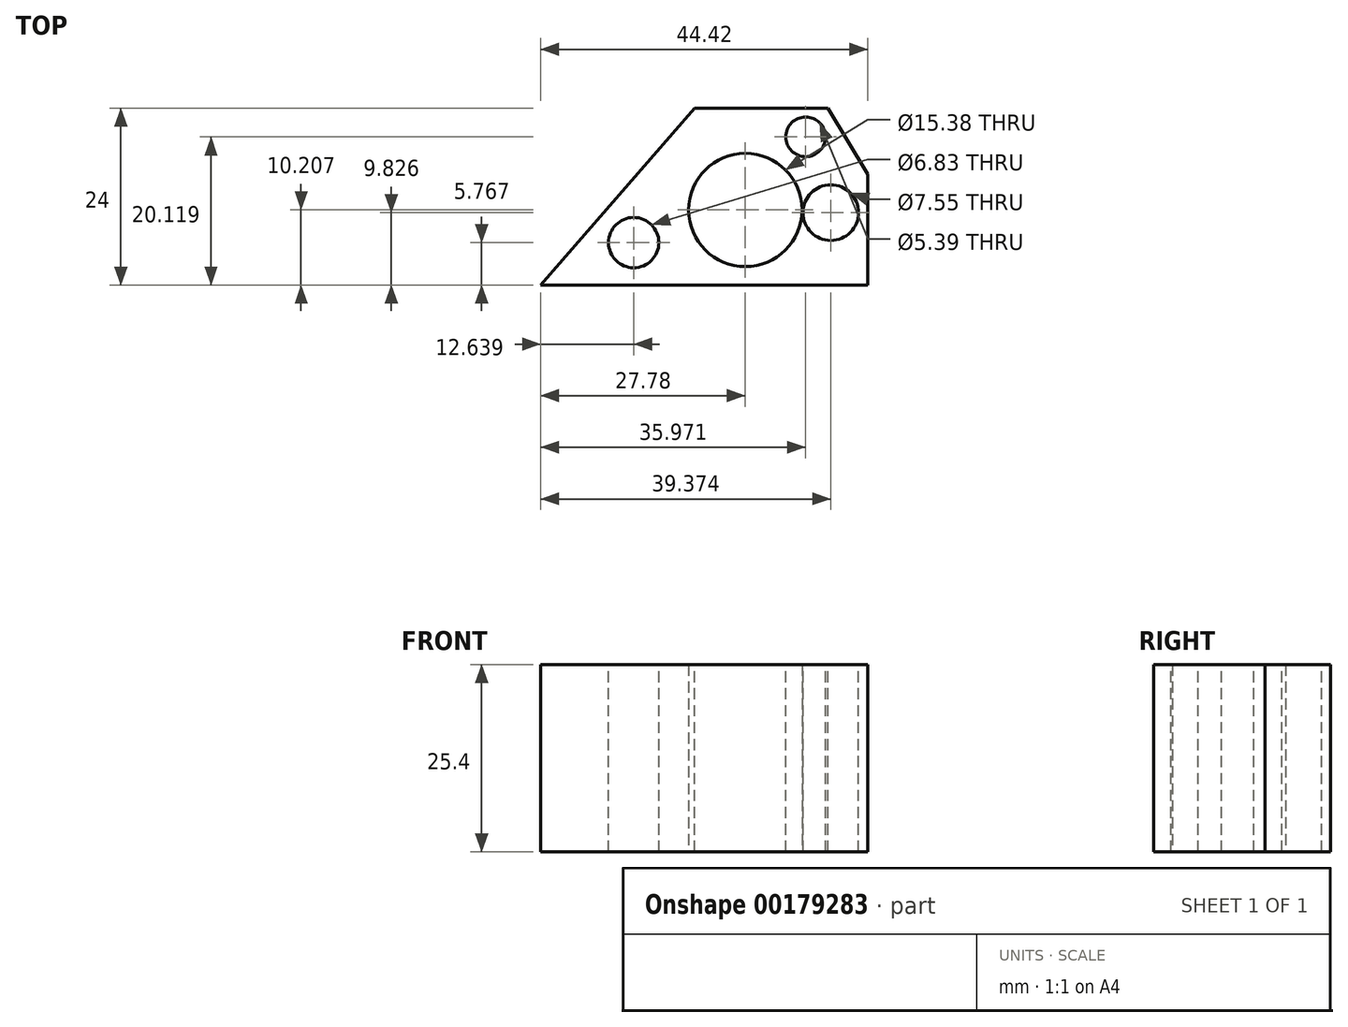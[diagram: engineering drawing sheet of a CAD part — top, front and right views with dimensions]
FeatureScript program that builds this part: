
annotation { "Feature Type Name" : "Feature", "Feature Type Description" : "" }
export const myFeature = defineFeature(function(context is Context, id is Id, definition is map)
    precondition{}
    {
        {
            var Q0;
            Q0=qCreatedBy(makeId("Top.planeOp"),FACE);
            var sketch = newSketch(context, id + "F0", { "sketchPlane" : qUnion([Q0])});
            skLineSegment(sketch, "E0", {"start": v(0, 0) * mm, "end": v(20.89, 24) * mm});
            skLineSegment(sketch, "E1", {"start": v(20.89, 24) * mm, "end": v(39.01, 24) * mm});
            skLineSegment(sketch, "E2", {"start": v(39.01, 24) * mm, "end": v(44.42, 15.08) * mm});
            skLineSegment(sketch, "E3", {"start": v(44.42, 15.08) * mm, "end": v(44.42, 0) * mm});
            skLineSegment(sketch, "E4", {"start": v(44.42, 0) * mm, "end": v(0, 0) * mm});
            skSolve(sketch);
        }
        {
            var Q0;
            Q0=makeQuery(id+"F0.imprint","IMPRINT",FACE,{"disambiguationData":[TD([[makeQuery(id+"F0.imprint","IMPRINT",EDGE,{"derivedFrom":sQuery(id+"F0.wireOp",EDGE,"E0")}),-1.0]])]});
            extrude(context, id + "F1", {"entities" : qUnion([Q0]), "oppositeDirection" : true, "depth" : 25.4 * mm});
        }
        {
            var Q0;
            Q0=makeQuery(id+"F1.opExtrude","CAP_FACE",FACE,{"disambiguationData":[OSD([sQuery(id+"F0.wireOp",EDGE,"E0"),sQuery(id+"F0.wireOp",EDGE,"E1"),sQuery(id+"F0.wireOp",EDGE,"E2"),sQuery(id+"F0.wireOp",EDGE,"E3"),sQuery(id+"F0.wireOp",EDGE,"E4")])],"isStart":false});
            var sketch = newSketch(context, id + "F2", { "sketchPlane" : qUnion([Q0])});
            skCircle(sketch, "E5", {"center": v(27.78, -10.2) * mm, "radius": 7.7 * mm});
            skSolve(sketch);
        }
        {
            var Q0;
            Q0 = qSketchRegion(id + "F2", true);
            extrude(context, id + "F3", {"entities" : qUnion([Q0]), "operationType" : NewBodyOperationType.REMOVE, "oppositeDirection" : true, "depth" : 25.4 * mm});
        }
        {
            var Q0;
            Q0=makeQuery(id+"F1.opExtrude","CAP_FACE",FACE,{"disambiguationData":[OSD([sQuery(id+"F0.wireOp",EDGE,"E0"),sQuery(id+"F0.wireOp",EDGE,"E1"),sQuery(id+"F0.wireOp",EDGE,"E2"),sQuery(id+"F0.wireOp",EDGE,"E3"),sQuery(id+"F0.wireOp",EDGE,"E4")])],"isStart":true});
            var sketch = newSketch(context, id + "F4", { "sketchPlane" : qUnion([Q0])});
            skSolve(sketch);
        }
        {
            var Q0;
            Q0=makeQuery(id+"F4.imprint","IMPRINT",FACE,{"disambiguationData":[TD([[makeQuery(id+"F4.imprint","IMPRINT",EDGE,{"derivedFrom":makeQuery(id+"F1.opExtrude","CAP_EDGE",EDGE,{"disambiguationData":[OSD([sQuery(id+"F0.wireOp",EDGE,"E0")])],"isStart":true})}),-1.0]])]});
            var sketch = newSketch(context, id + "F5", { "sketchPlane" : qUnion([Q0])});
            skCircle(sketch, "E6", {"center": v(35.97, 20.12) * mm, "radius": 2.7 * mm});
            skCircle(sketch, "E7", {"center": v(39.37, 9.83) * mm, "radius": 3.77 * mm});
            skCircle(sketch, "E8", {"center": v(12.64, 5.77) * mm, "radius": 3.41 * mm});
            skSolve(sketch);
        }
        {
            var Q0;
            Q0 = qSketchRegion(id + "F5", true);
            extrude(context, id + "F6", {"entities" : qUnion([Q0]), "operationType" : NewBodyOperationType.REMOVE, "oppositeDirection" : true, "depth" : 25.4 * mm});
        }
    });
